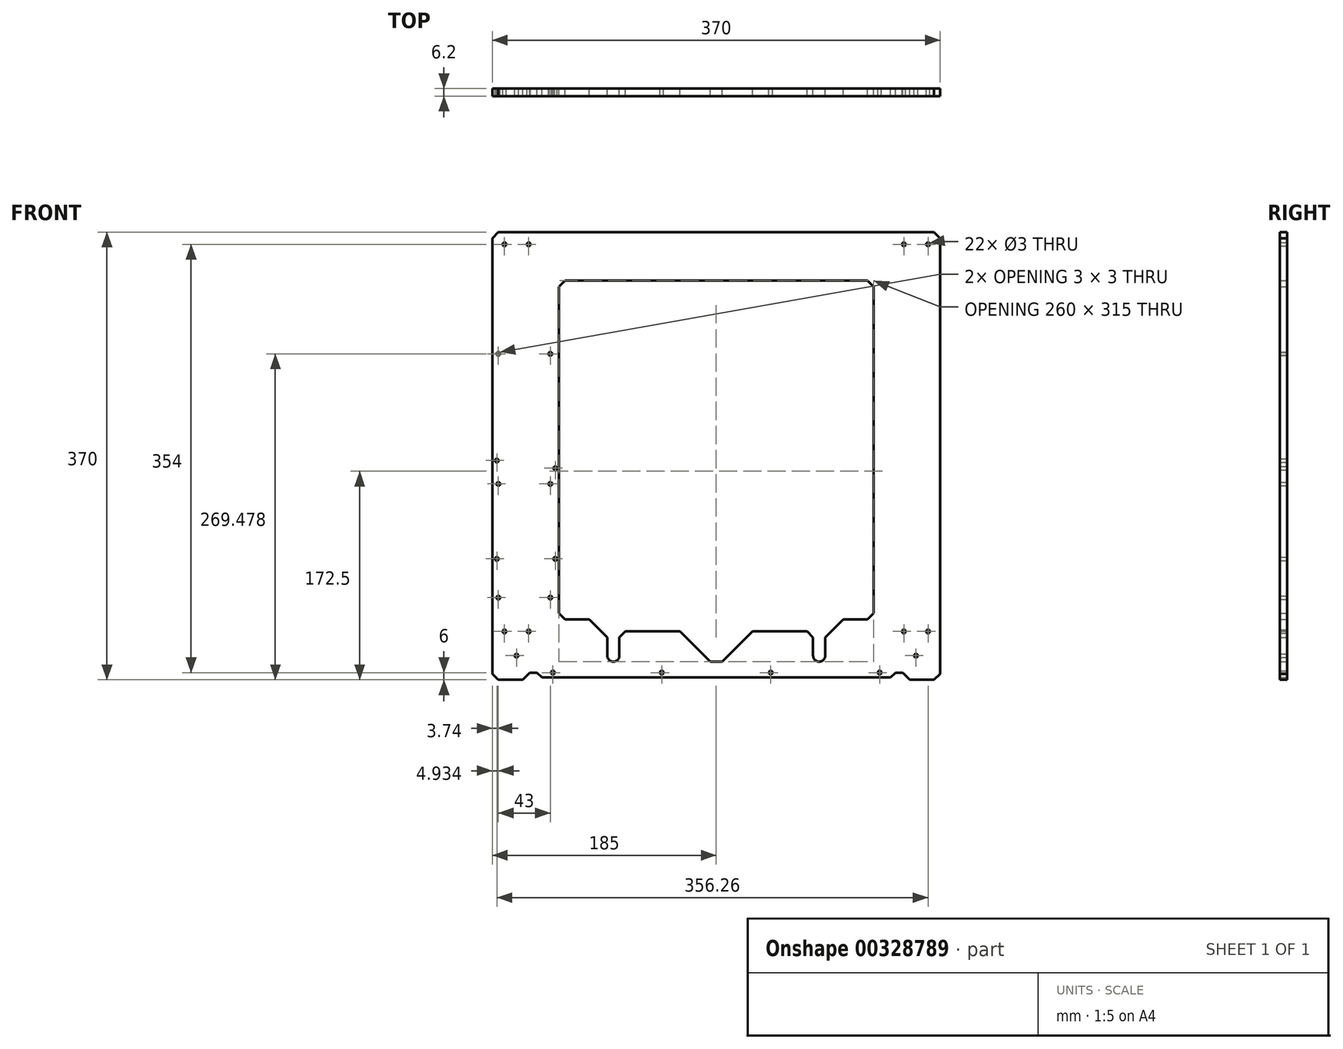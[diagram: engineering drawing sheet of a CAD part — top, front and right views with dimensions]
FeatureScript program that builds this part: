
annotation { "Feature Type Name" : "Feature", "Feature Type Description" : "" }
export const myFeature = defineFeature(function(context is Context, id is Id, definition is map)
    precondition{}
    {
        {
            var Q0;
            Q0=qCreatedBy(makeId("Front.planeOp"),FACE);
            var sketch = newSketch(context, id + "F0", { "sketchPlane" : qUnion([Q0])});
            skLineSegment(sketch, "E0", {"start": v(-180, -185) * mm, "end": v(-185, -180.2) * mm});
            skLineSegment(sketch, "E1", {"start": v(-185, -180.2) * mm, "end": v(-185, 180) * mm});
            skLineSegment(sketch, "E2", {"start": v(-185, 180) * mm, "end": v(-180, 185) * mm});
            skLineSegment(sketch, "E3", {"start": v(-180, 185) * mm, "end": v(180, 185) * mm});
            skLineSegment(sketch, "E4", {"start": v(180, 185) * mm, "end": v(185, 180) * mm});
            skLineSegment(sketch, "E5", {"start": v(185, 180) * mm, "end": v(185, -180) * mm});
            skLineSegment(sketch, "E6", {"start": v(185, -180) * mm, "end": v(180, -185) * mm});
            skLineSegment(sketch, "E7", {"start": v(180, -185) * mm, "end": v(160, -185) * mm});
            skLineSegment(sketch, "E8", {"start": v(160, -185) * mm, "end": v(158, -183) * mm});
            skLineSegment(sketch, "E9", {"start": v(144, -183) * mm, "end": v(-144, -183) * mm});
            skLineSegment(sketch, "E10", {"start": v(-158, -183) * mm, "end": v(-160, -185) * mm});
            skLineSegment(sketch, "E11", {"start": v(-160, -185) * mm, "end": v(-180, -185) * mm});
            skArc(sketch, "E12", {"start": v(-90, -165) * mm, "mid": v(-85, -170) * mm, "end": v(-80, -165) * mm});
            skLineSegment(sketch, "E13", {"start": v(-90, -165) * mm, "end": v(-90, -150) * mm});
            skLineSegment(sketch, "E14", {"start": v(-90, -150) * mm, "end": v(-105, -135) * mm});
            skLineSegment(sketch, "E15", {"start": v(-105, -135) * mm, "end": v(-125, -135) * mm});
            skLineSegment(sketch, "E16", {"start": v(-125, -135) * mm, "end": v(-130, -130) * mm});
            skLineSegment(sketch, "E17", {"start": v(-130, -130) * mm, "end": v(-130, 140) * mm});
            skLineSegment(sketch, "E18", {"start": v(-130, 140) * mm, "end": v(-125, 145) * mm});
            skLineSegment(sketch, "E19", {"start": v(-125, 145) * mm, "end": v(125, 145) * mm});
            skLineSegment(sketch, "E20", {"start": v(125, 145) * mm, "end": v(130, 140) * mm});
            skLineSegment(sketch, "E21", {"start": v(130, 140) * mm, "end": v(130, -130) * mm});
            skLineSegment(sketch, "E22", {"start": v(130, -130) * mm, "end": v(125, -135) * mm});
            skLineSegment(sketch, "E23", {"start": v(-80, -165) * mm, "end": v(-80, -150) * mm});
            skLineSegment(sketch, "E24", {"start": v(-80, -150) * mm, "end": v(-75, -145) * mm});
            skArc(sketch, "E25", {"start": v(80, -165) * mm, "mid": v(85, -170) * mm, "end": v(90, -165) * mm});
            skLineSegment(sketch, "E26", {"start": v(125, -135) * mm, "end": v(105, -135) * mm});
            skLineSegment(sketch, "E27", {"start": v(105, -135) * mm, "end": v(90, -150) * mm});
            skLineSegment(sketch, "E28", {"start": v(90, -150) * mm, "end": v(90, -165) * mm});
            skLineSegment(sketch, "E29", {"start": v(80, -165) * mm, "end": v(80, -150) * mm});
            skLineSegment(sketch, "E30", {"start": v(80, -150) * mm, "end": v(75, -145) * mm});
            skLineSegment(sketch, "E31", {"start": v(-5, -170) * mm, "end": v(5, -170) * mm});
            skLineSegment(sketch, "E32", {"start": v(5, -170) * mm, "end": v(30, -145) * mm});
            skLineSegment(sketch, "E33", {"start": v(-5, -170) * mm, "end": v(-30, -145) * mm});
            skLineSegment(sketch, "E34", {"start": v(-75, -145) * mm, "end": v(-30, -145) * mm});
            skLineSegment(sketch, "E35", {"start": v(30, -145) * mm, "end": v(75, -145) * mm});
            skCircle(sketch, "E36", {"center": v(-181.26, -3.72) * mm, "radius": 1.5 * mm});
            skCircle(sketch, "E37", {"center": v(-133, -10.07) * mm, "radius": 1.5 * mm});
            skCircle(sketch, "E38", {"center": v(-133, -85) * mm, "radius": 1.5 * mm});
            skCircle(sketch, "E39", {"center": v(-181.26, -85) * mm, "radius": 1.5 * mm});
            skLineSegment(sketch, "E40", {"start": v(158, -183) * mm, "end": v(154, -179) * mm});
            skLineSegment(sketch, "E41", {"start": v(154, -179) * mm, "end": v(148, -179) * mm});
            skLineSegment(sketch, "E42", {"start": v(148, -179) * mm, "end": v(144, -183) * mm});
            skLineSegment(sketch, "E43", {"start": v(-158, -183) * mm, "end": v(-154, -179) * mm});
            skLineSegment(sketch, "E44", {"start": v(-154, -179) * mm, "end": v(-148, -179) * mm});
            skLineSegment(sketch, "E45", {"start": v(-148, -179) * mm, "end": v(-144, -183) * mm});
            skCircle(sketch, "E46", {"center": v(-135, -179) * mm, "radius": 1.5 * mm});
            skCircle(sketch, "E47", {"center": v(135, -179) * mm, "radius": 1.5 * mm});
            skCircle(sketch, "E48", {"center": v(45, -179) * mm, "radius": 1.5 * mm});
            skCircle(sketch, "E49", {"center": v(-45, -179) * mm, "radius": 1.5 * mm});
            skCircle(sketch, "E50", {"center": v(-175, -145) * mm, "radius": 1.5 * mm});
            skCircle(sketch, "E51", {"center": v(-155, -145) * mm, "radius": 1.5 * mm});
            skCircle(sketch, "E52", {"center": v(-165, -165) * mm, "radius": 1.5 * mm});
            skCircle(sketch, "E53", {"center": v(165, -165) * mm, "radius": 1.5 * mm});
            skCircle(sketch, "E54", {"center": v(155, -145) * mm, "radius": 1.5 * mm});
            skCircle(sketch, "E55", {"center": v(175, -145) * mm, "radius": 1.5 * mm});
            skCircle(sketch, "E56", {"center": v(175, 175) * mm, "radius": 1.5 * mm});
            skCircle(sketch, "E57", {"center": v(155, 175) * mm, "radius": 1.5 * mm});
            skCircle(sketch, "E58", {"center": v(-175, 175) * mm, "radius": 1.5 * mm});
            skCircle(sketch, "E59", {"center": v(-155, 175) * mm, "radius": 1.5 * mm});
            skCircle(sketch, "E60", {"center": v(-137.05, -117.03) * mm, "radius": 1.5 * mm});
            skCircle(sketch, "E61", {"center": v(-180.05, -23.03) * mm, "radius": 1.5 * mm});
            skCircle(sketch, "E62", {"center": v(-137.05, -23.03) * mm, "radius": 1.5 * mm});
            skCircle(sketch, "E63", {"center": v(-180.05, 84.47) * mm, "radius": 1.5 * mm});
            skCircle(sketch, "E64", {"center": v(-137.05, 84.47) * mm, "radius": 1.5 * mm});
            skCircle(sketch, "E65", {"center": v(-180.08, -117) * mm, "radius": 1.5 * mm});
            skCircle(sketch, "E66", {"center": v(-180.08, 84.5) * mm, "radius": 1.5 * mm});
            skCircle(sketch, "E67", {"center": v(-137.08, 84.5) * mm, "radius": 1.5 * mm});
            skLineSegment(sketch, "E68", {"start": v(0, 185) * mm, "end": v(0, -183) * mm, "construction": true});
            skLineSegment(sketch, "E69", {"start": v(185, 0) * mm, "end": v(-185, 0) * mm, "construction": true});
            skSolve(sketch);
        }
        {
            var Q0;
            Q0=qSketchRegion(id+"F0",true);
            extrude(context, id + "F1", {"entities" : qUnion([Q0]), "depth" : 6.2 * mm});
        }
    });
